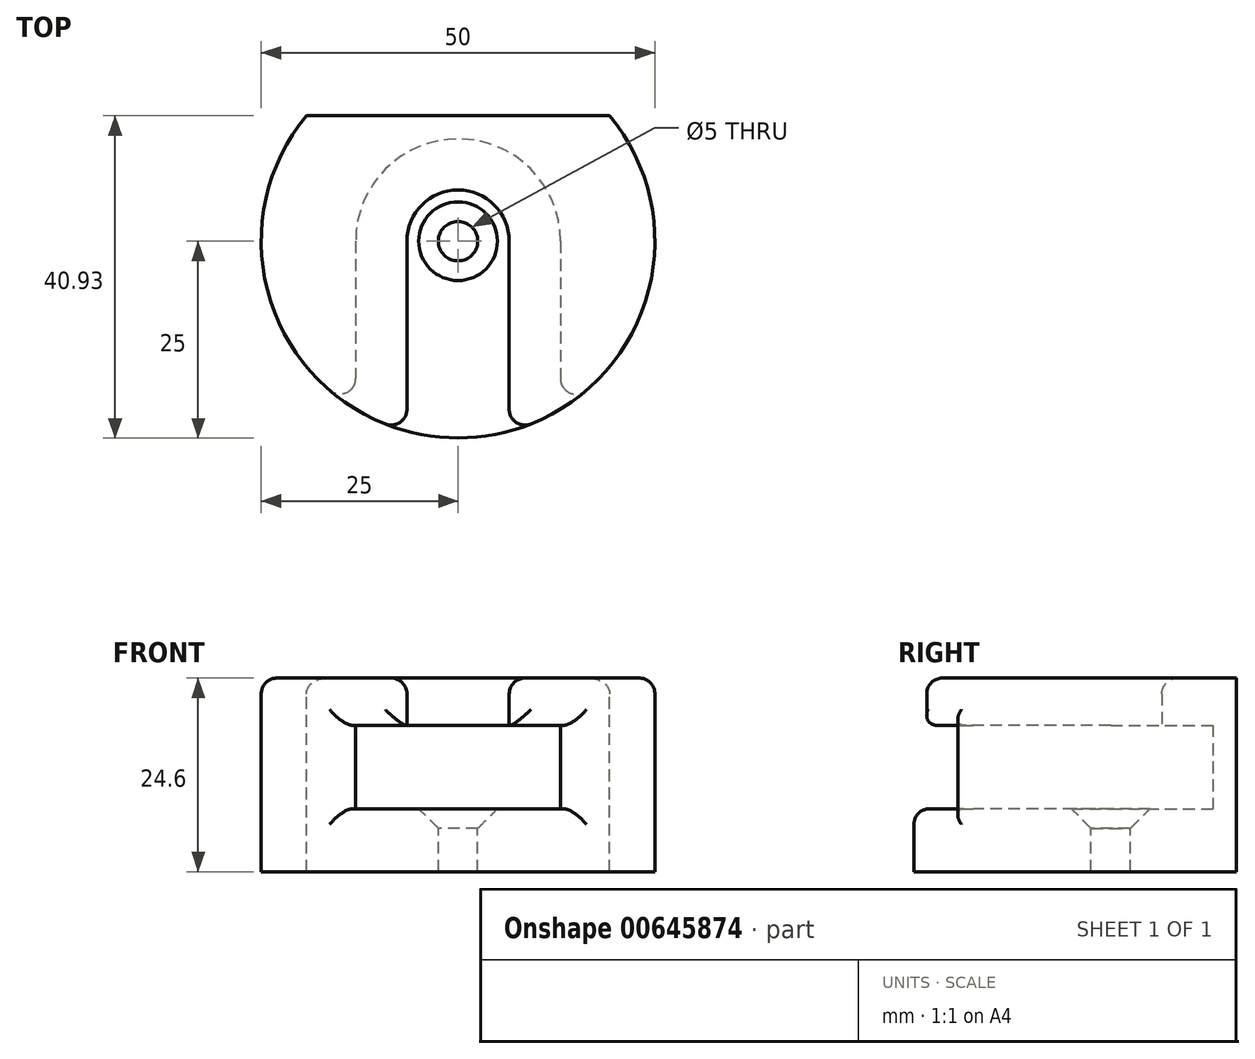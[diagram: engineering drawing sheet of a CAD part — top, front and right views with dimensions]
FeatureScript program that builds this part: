
annotation { "Feature Type Name" : "Feature", "Feature Type Description" : "" }
export const myFeature = defineFeature(function(context is Context, id is Id, definition is map)
    precondition{}
    {
        {
            var Q0;
            Q0=qCreatedBy(makeId("Top.planeOp"),FACE);
            cPlane(context, id + "F0", {"entities" : qUnion([Q0]), "cplaneType" : CPlaneType.OFFSET, "offset" : 8 * mm, "width" : 150 * mm, "height" : 150 * mm});
        }
        {
            var Q0;
            Q0=qCreatedBy(id+"F0.planeOp",FACE);
            cPlane(context, id + "F1", {"entities" : qUnion([Q0]), "cplaneType" : CPlaneType.OFFSET, "offset" : 10.6 * mm, "width" : 150 * mm, "height" : 150 * mm});
        }
        {
            var Q0;
            Q0=qCreatedBy(makeId("Top.planeOp"),FACE);
            var Q1;
            Q1=qCreatedBy(makeId("Top.planeOp"),FACE);
            var Q2;
            Q2=qCreatedBy(makeId("Top.planeOp"),FACE);
            var sketch = newSketch(context, id + "F2", { "sketchPlane" : qUnion([Q0, Q1, Q2])});
            skCircle(sketch, "E0", {"center": v(0, 0) * mm, "radius": 25 * mm});
            skSolve(sketch);
        }
        {
            var Q0;
            Q0=makeQuery(id+"F2.imprint","IMPRINT",FACE,{"disambiguationData":[TD([[makeQuery(id+"F2.imprint","IMPRINT",EDGE,{"derivedFrom":sQuery(id+"F2.wireOp",EDGE,"E0")}),1.0]])]});
            extrude(context, id + "F3", {"entities" : qUnion([Q0]), "depth" : 8 * mm, "offsetDistance" : 25 * mm});
        }
        {
            var Q0;
            Q0=qCreatedBy(id+"F0.planeOp",FACE);
            var sketch = newSketch(context, id + "F4", { "sketchPlane" : qUnion([Q0])});
            skPoint(sketch, "E1", {"position": v(0, 0) * mm});
            skSolve(sketch);
        }
        {
            var Q0;
            Q0=sQuery(id+"F4.wireOp",VERTEX,"E1");
            var Q1;
            Q1=makeQuery(id+"F3.opExtrude","SWEPT_BODY",BODY,{"disambiguationData":[OSD([sQuery(id+"F2.wireOp",EDGE,"E0")])]});
            hole(context, id + "F5", {"style" : HoleStyle.C_SINK, "endStyle" : HoleEndStyle.THROUGH, "holeDiameter" : 5 * mm, "cSinkDiameter" : 10 * mm, "cSinkAngle" : 90 * degree, "majorDiameter" : 5 * mm, "isTappedThrough" : true, "tappedDepth" : 12 * mm, "tapClearance" : 3, "locations" : qUnion([Q0]), "scope" : qUnion([Q1])});
        }
        {
            var Q0;
            Q0=qCreatedBy(id+"F0.planeOp",FACE);
            var sketch = newSketch(context, id + "F6", { "sketchPlane" : qUnion([Q0])});
            skCircle(sketch, "E2", {"center": v(0, 0) * mm, "radius": 13 * mm});
            skCircle(sketch, "E3", {"center": v(0, 0) * mm, "radius": 25 * mm});
            skLineSegment(sketch, "E4", {"start": v(-13, 0) * mm, "end": v(-13, -21.35) * mm});
            skLineSegment(sketch, "E5", {"start": v(13, 0) * mm, "end": v(13, -21.35) * mm});
            skSolve(sketch);
        }
        {
            var Q0;
            {var subQ0=sQuery(id+"F6.wireOp",EDGE,"E4");Q0=makeQuery(id+"F6.imprint","IMPRINT",FACE,{"disambiguationData":[TD([[makeQuery(id+"F6.imprint","IMPRINT",EDGE,{"derivedFrom":subQ0}),-1.0]])]});}
            extrude(context, id + "F7", {"entities" : qUnion([Q0]), "operationType" : NewBodyOperationType.ADD, "depth" : 10.6 * mm, "offsetDistance" : 25 * mm});
        }
        {
            var Q0;
            Q0=qCreatedBy(id+"F1.planeOp",FACE);
            var sketch = newSketch(context, id + "F8", { "sketchPlane" : qUnion([Q0])});
            skCircle(sketch, "E6", {"center": v(0, 0) * mm, "radius": 6.5 * mm});
            skCircle(sketch, "E7", {"center": v(0, 0) * mm, "radius": 25 * mm});
            skLineSegment(sketch, "E8", {"start": v(-6.5, 0) * mm, "end": v(-6.5, -24.14) * mm});
            skLineSegment(sketch, "E9", {"start": v(6.5, 0) * mm, "end": v(6.5, -24.14) * mm});
            skSolve(sketch);
        }
        {
            var Q0;
            {var subQ0=sQuery(id+"F8.wireOp",EDGE,"E8");Q0=makeQuery(id+"F8.imprint","IMPRINT",FACE,{"disambiguationData":[TD([[makeQuery(id+"F8.imprint","IMPRINT",EDGE,{"derivedFrom":subQ0}),-1.0]])]});}
            extrude(context, id + "F9", {"entities" : qUnion([Q0]), "operationType" : NewBodyOperationType.ADD, "depth" : 6 * mm, "offsetDistance" : 25 * mm});
        }
        {
            var Q0;
            Q0=makeQuery(id+"F9.opExtrude","CAP_FACE",FACE,{"disambiguationData":[OSD([sQuery(id+"F8.wireOp",EDGE,"E6"),sQuery(id+"F8.wireOp",EDGE,"E7"),sQuery(id+"F8.wireOp",EDGE,"E8"),sQuery(id+"F8.wireOp",EDGE,"E9")])],"isStart":false});
            var sketch = newSketch(context, id + "F10", { "sketchPlane" : qUnion([Q0])});
            skCircle(sketch, "E10", {"center": v(0, 0) * mm, "radius": 25 * mm});
            skLineSegment(sketch, "E11", {"start": v(-19.26, 15.93) * mm, "end": v(19.26, 15.93) * mm});
            skSolve(sketch);
        }
        {
            var Q0;
            {var subQ0=sQuery(id+"F10.wireOp",EDGE,"E11");Q0=makeQuery(id+"F10.imprint","IMPRINT",FACE,{"disambiguationData":[TD([[makeQuery(id+"F10.imprint","IMPRINT",EDGE,{"derivedFrom":subQ0}),1.0]])]});}
            extrude(context, id + "F11", {"entities" : qUnion([Q0]), "operationType" : NewBodyOperationType.REMOVE, "endBound" : BoundingType.THROUGH_ALL, "oppositeDirection" : true, "depth" : 25 * mm, "offsetDistance" : 25 * mm});
        }
        {
            var Q0;
            {var subQ0=sQuery(id+"F8.wireOp",EDGE,"E7");var subQ1=sQuery(id+"F8.wireOp",EDGE,"E9");Q0=makeQuery(id+"F11.boolean.opBoolean","SPLIT",EDGE,{"disambiguationData":[TD([makeQuery(id+"F9.opExtrude","SWEPT_FACE",FACE,{"disambiguationData":[OSD([subQ1])]})])],"derivedFrom":makeQuery(id+"F9.opExtrude","CAP_EDGE",EDGE,{"disambiguationData":[OSD([subQ0])],"isStart":false})});}
            var Q1;
            {var subQ0=sQuery(id+"F8.wireOp",EDGE,"E7");var subQ1=sQuery(id+"F8.wireOp",EDGE,"E8");Q1=makeQuery(id+"F11.boolean.opBoolean","SPLIT",EDGE,{"disambiguationData":[TD([makeQuery(id+"F9.opExtrude","SWEPT_FACE",FACE,{"disambiguationData":[OSD([subQ1])]})])],"derivedFrom":makeQuery(id+"F9.opExtrude","CAP_EDGE",EDGE,{"disambiguationData":[OSD([subQ0])],"isStart":false})});}
            var Q2;
            Q2=makeQuery(id+"F9.opExtrude","CAP_EDGE",EDGE,{"disambiguationData":[OSD([sQuery(id+"F8.wireOp",EDGE,"E8")])],"isStart":false});
            var Q3;
            {var subQ1=sQuery(id+"F8.wireOp",EDGE,"E7");Q3=makeQuery(id+"F9.boolean.opBoolean","SPLIT",EDGE,{"disambiguationData":[TD([makeQuery(id+"F7.opExtrude","SWEPT_FACE",FACE,{"disambiguationData":[OSD([sQuery(id+"F6.wireOp",EDGE,"E5")])]})])],"derivedFrom":makeQuery(id+"F9.opExtrude","CAP_EDGE",EDGE,{"disambiguationData":[OSD([subQ1])],"isStart":true})});}
            var Q4;
            Q4=makeQuery(id+"F9.opExtrude","SWEPT_EDGE",EDGE,{"disambiguationData":[OSD([sQuery(id+"F8.wireOp",EDGE,"E7"),sQuery(id+"F8.wireOp",EDGE,"E9")])]});
            var Q5;
            Q5=makeQuery(id+"F9.opExtrude","SWEPT_EDGE",EDGE,{"disambiguationData":[OSD([sQuery(id+"F8.wireOp",EDGE,"E7"),sQuery(id+"F8.wireOp",EDGE,"E8")])]});
            var Q6;
            Q6=makeQuery(id+"F3.opExtrude","CAP_EDGE",EDGE,{"disambiguationData":[OSD([sQuery(id+"F2.wireOp",EDGE,"E0")])],"isStart":false});
            var Q7;
            Q7=makeQuery(id+"F7.opExtrude","SWEPT_EDGE",EDGE,{"disambiguationData":[OSD([sQuery(id+"F6.wireOp",EDGE,"E3"),sQuery(id+"F6.wireOp",EDGE,"E5")])]});
            var Q8;
            Q8=makeQuery(id+"F7.opExtrude","SWEPT_EDGE",EDGE,{"disambiguationData":[OSD([sQuery(id+"F6.wireOp",EDGE,"E3"),sQuery(id+"F6.wireOp",EDGE,"E4")])]});
            var Q9;
            {var subQ1=sQuery(id+"F8.wireOp",EDGE,"E7");Q9=makeQuery(id+"F9.boolean.opBoolean","SPLIT",EDGE,{"disambiguationData":[TD([makeQuery(id+"F7.opExtrude","SWEPT_FACE",FACE,{"disambiguationData":[OSD([sQuery(id+"F6.wireOp",EDGE,"E4")])]})])],"derivedFrom":makeQuery(id+"F9.opExtrude","CAP_EDGE",EDGE,{"disambiguationData":[OSD([subQ1])],"isStart":true})});}
            var Q10;
            Q10=makeQuery(id+"F11.boolean.opBoolean","COPY",EDGE,{"derivedFrom":makeQuery(id+"F11.opExtrude","CAP_EDGE",EDGE,{"disambiguationData":[OSD([sQuery(id+"F10.wireOp",EDGE,"E11")])],"isStart":true})});
            var Q11;
            {var subQ0=sQuery(id+"F10.wireOp",EDGE,"E11");var subQ1=sQuery(id+"F10.wireOp",EDGE,"E10");Q11=makeQuery(id+"F11.boolean.opBoolean","COPY",EDGE,{"derivedFrom":makeQuery(id+"F11.opExtrude","SWEPT_EDGE",EDGE,{"disambiguationData":[OSD([subQ1,subQ0]),TDD([makeQuery(id+"F10.imprint","INTERSECT",VERTEX,{"disambiguationData":[OD(1.0)],"derivedFrom":[subQ1,subQ0]})])]})});}
            var Q12;
            {var subQ0=sQuery(id+"F10.wireOp",EDGE,"E11");var subQ1=sQuery(id+"F10.wireOp",EDGE,"E10");Q12=makeQuery(id+"F11.boolean.opBoolean","COPY",EDGE,{"derivedFrom":makeQuery(id+"F11.opExtrude","SWEPT_EDGE",EDGE,{"disambiguationData":[OSD([subQ1,subQ0]),TDD([makeQuery(id+"F10.imprint","INTERSECT",VERTEX,{"disambiguationData":[OD(0.0)],"derivedFrom":[subQ1,subQ0]})])]})});}
            fillet(context, id + "F12", {"entities" : qUnion([Q0, Q1, Q2, Q3, Q4, Q5, Q6, Q7, Q8, Q9, Q10, Q11, Q12]), "radius" : 2 * mm, "tangentPropagation" : true, "allowEdgeOverflow" : false});
        }
    });
